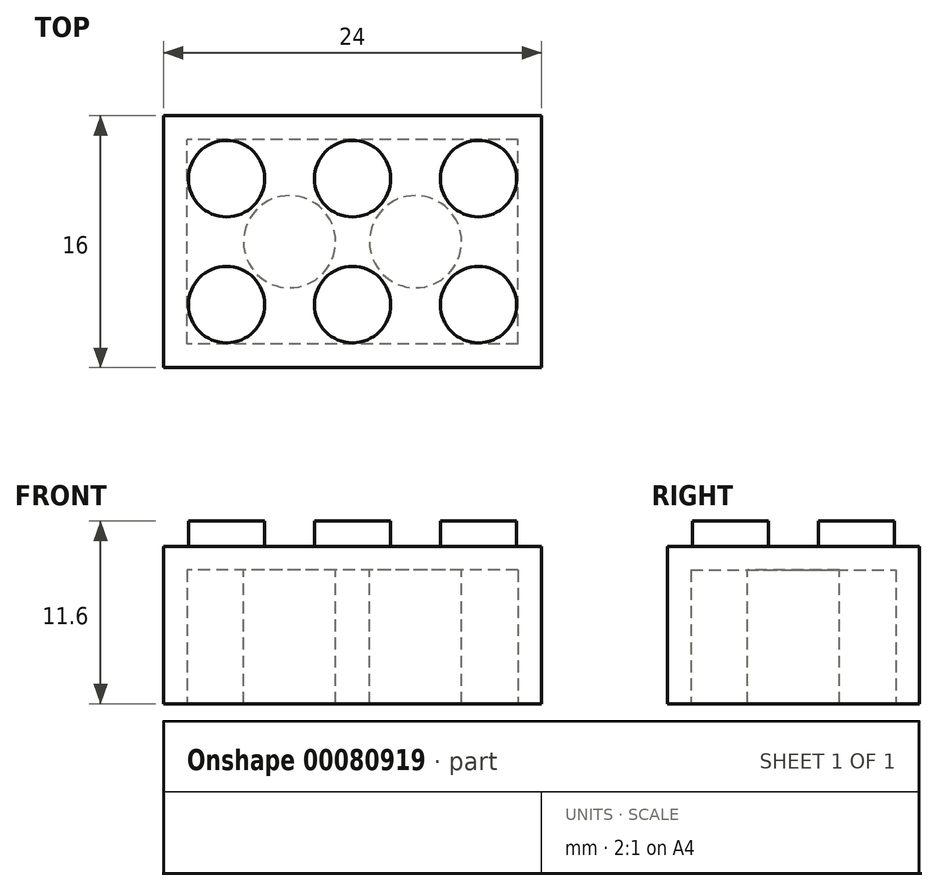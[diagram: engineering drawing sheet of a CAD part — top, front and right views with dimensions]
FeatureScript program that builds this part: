
annotation { "Feature Type Name" : "Feature", "Feature Type Description" : "" }
export const myFeature = defineFeature(function(context is Context, id is Id, definition is map)
    precondition{}
    {
        {
            var Q0;
            Q0=qCreatedBy(makeId("Top.planeOp"),FACE);
            var sketch = newSketch(context, id + "F0", { "sketchPlane" : qUnion([Q0])});
            skLineSegment(sketch, "E0.bottom", {"start": v(12, -8) * mm, "end": v(-12, -8) * mm});
            skLineSegment(sketch, "E0.top", {"start": v(12, 8) * mm, "end": v(-12, 8) * mm});
            skLineSegment(sketch, "E0.left", {"start": v(12, -8) * mm, "end": v(12, 8) * mm});
            skLineSegment(sketch, "E0.right", {"start": v(-12, -8) * mm, "end": v(-12, 8) * mm});
            skPoint(sketch, "E0.middle", {"position": v(0, 0) * mm});
            skSolve(sketch);
        }
        {
            var Q0;
            Q0 = qSketchRegion(id + "F0", true);
            extrude(context, id + "F1", {"entities" : qUnion([Q0]), "depth" : 10 * mm});
        }
        {
            var Q0;
            Q0=makeQuery(id+"F1.opExtrude","CAP_FACE",FACE,{"disambiguationData":[OSD([sQuery(id+"F0.wireOp",EDGE,"E0.bottom"),sQuery(id+"F0.wireOp",EDGE,"E0.top"),sQuery(id+"F0.wireOp",EDGE,"E0.left"),sQuery(id+"F0.wireOp",EDGE,"E0.right")])],"isStart":true});
            shell(context, id + "F2", {"entities" : qUnion([Q0]), "thickness" : 1.5 * mm});
        }
        {
            var Q0;
            Q0=makeQuery(id+"F1.opExtrude","CAP_FACE",FACE,{"disambiguationData":[OSD([sQuery(id+"F0.wireOp",EDGE,"E0.bottom"),sQuery(id+"F0.wireOp",EDGE,"E0.top"),sQuery(id+"F0.wireOp",EDGE,"E0.left"),sQuery(id+"F0.wireOp",EDGE,"E0.right")])],"isStart":false});
            var sketch = newSketch(context, id + "F3", { "sketchPlane" : qUnion([Q0])});
            skCircle(sketch, "E1", {"center": v(-8, -4) * mm, "radius": 2.43 * mm});
            skCircle(sketch, "E2.0.1.0", {"center": v(-8, 4) * mm, "radius": 2.43 * mm});
            skCircle(sketch, "E2.1.0.0", {"center": v(0, -4) * mm, "radius": 2.43 * mm});
            skCircle(sketch, "E2.1.1.0", {"center": v(0, 4) * mm, "radius": 2.43 * mm});
            skCircle(sketch, "E2.2.0.0", {"center": v(8, -4) * mm, "radius": 2.43 * mm});
            skCircle(sketch, "E2.2.1.0", {"center": v(8, 4) * mm, "radius": 2.43 * mm});
            skLineSegment(sketch, "E2.direction1", {"start": v(-8, -4) * mm, "end": v(0, -4) * mm, "construction": true});
            skLineSegment(sketch, "E2.direction2", {"start": v(-8, -4) * mm, "end": v(-8, 4) * mm, "construction": true});
            skSolve(sketch);
        }
        {
            var Q0;
            Q0 = qSketchRegion(id + "F3", true);
            extrude(context, id + "F4", {"entities" : qUnion([Q0]), "operationType" : NewBodyOperationType.ADD, "depth" : 1.6 * mm});
        }
        {
            var Q0;
            Q0=makeQuery(id+"F1.opExtrude","CAP_FACE",FACE,{"disambiguationData":[OSD([sQuery(id+"F0.wireOp",EDGE,"E0.bottom"),sQuery(id+"F0.wireOp",EDGE,"E0.top"),sQuery(id+"F0.wireOp",EDGE,"E0.left"),sQuery(id+"F0.wireOp",EDGE,"E0.right")])],"isStart":false});
            var sketch = newSketch(context, id + "F5", { "sketchPlane" : qUnion([Q0])});
            skCircle(sketch, "E3", {"center": v(-4, 0) * mm, "radius": 2.93 * mm});
            skCircle(sketch, "E4", {"center": v(4, 0) * mm, "radius": 2.93 * mm});
            skSolve(sketch);
        }
        {
            var Q0;
            Q0 = qSketchRegion(id + "F5", true);
            extrude(context, id + "F6", {"entities" : qUnion([Q0]), "operationType" : NewBodyOperationType.ADD, "oppositeDirection" : true, "depth" : 10 * mm});
        }
    });
